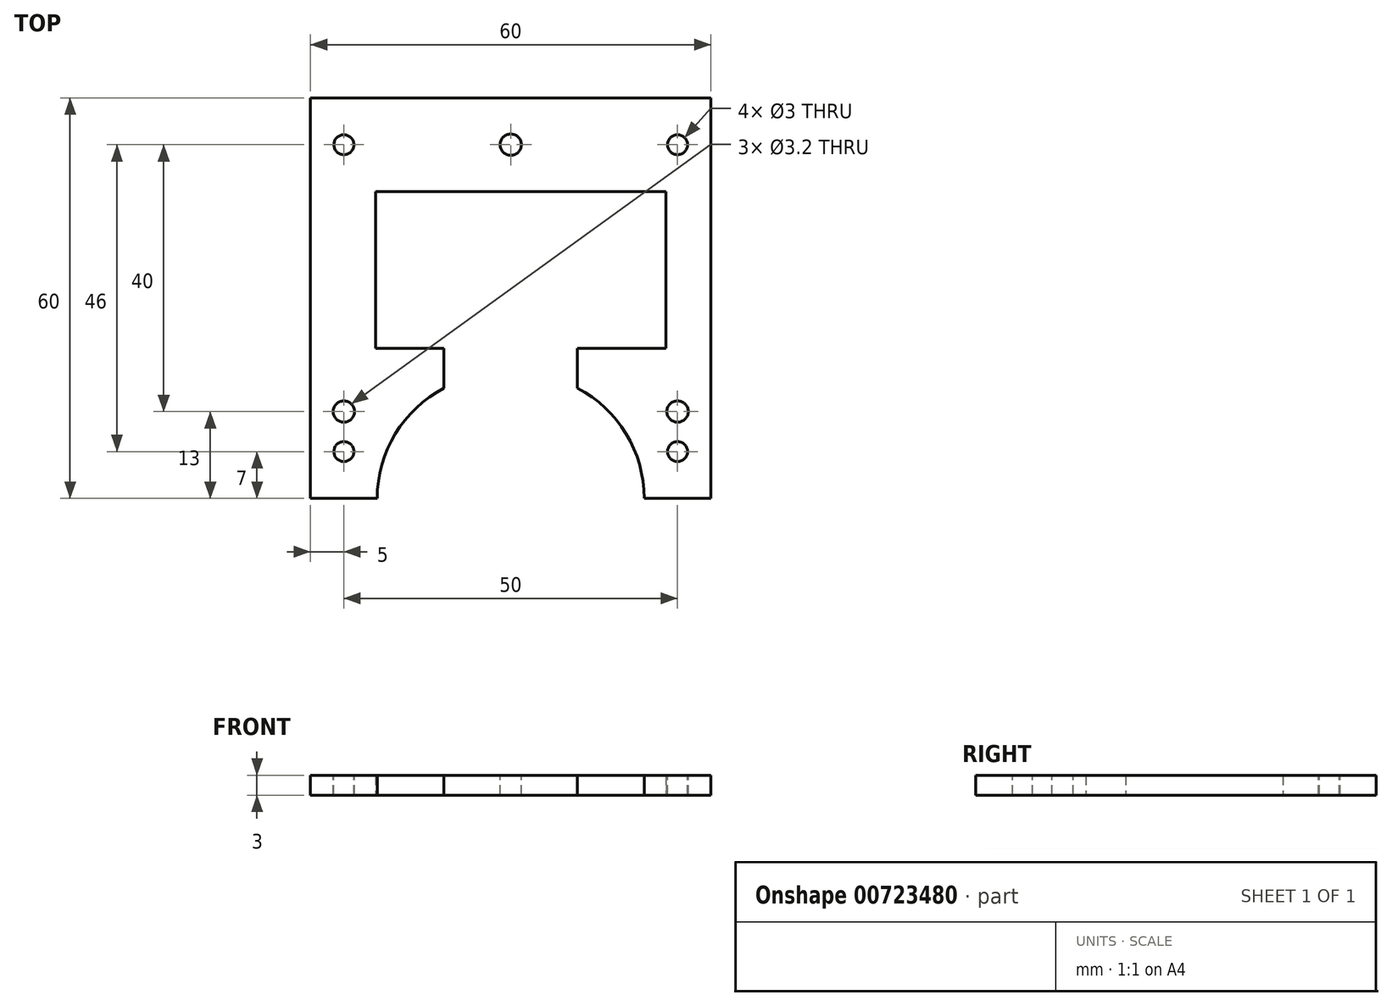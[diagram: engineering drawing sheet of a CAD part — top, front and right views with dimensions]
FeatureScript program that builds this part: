
annotation { "Feature Type Name" : "Feature", "Feature Type Description" : "" }
export const myFeature = defineFeature(function(context is Context, id is Id, definition is map)
    precondition{}
    {
        {
            var Q0;
            Q0=qCreatedBy(makeId("Top.planeOp"),FACE);
            var sketch = newSketch(context, id + "F0", { "sketchPlane" : qUnion([Q0])});
            skLineSegment(sketch, "E0.bottom", {"start": v(30, 30) * mm, "end": v(-30, 30) * mm});
            skLineSegment(sketch, "E0.top", {"start": v(30, -30) * mm, "end": v(20, -30) * mm});
            skLineSegment(sketch, "E0.left", {"start": v(30, 30) * mm, "end": v(30, -30) * mm});
            skLineSegment(sketch, "E0.right", {"start": v(-30, 30) * mm, "end": v(-30, -30) * mm});
            skPoint(sketch, "E0.middle", {"position": v(0, 0) * mm});
            skLineSegment(sketch, "E1.bottom", {"start": v(20, 15.5) * mm, "end": v(-20, 15.5) * mm});
            skLineSegment(sketch, "E1.left", {"start": v(20, 15.5) * mm, "end": v(20, -7.5) * mm});
            skLineSegment(sketch, "E1.right", {"start": v(-20, 15.5) * mm, "end": v(-20, -7.5) * mm});
            skLineSegment(sketch, "E2", {"start": v(-20, -7.5) * mm, "end": v(-10, -7.5) * mm});
            skLineSegment(sketch, "E3", {"start": v(10, -7.5) * mm, "end": v(20, -7.5) * mm});
            skPoint(sketch, "E4.orphan", {"position": v(-20, -15.5) * mm});
            skPoint(sketch, "E5.orphan", {"position": v(20, -15.5) * mm});
            skLineSegment(sketch, "E6", {"start": v(-20, -15.5) * mm, "end": v(-20, -30) * mm});
            skLineSegment(sketch, "E7", {"start": v(20, -30) * mm, "end": v(20, -15.5) * mm});
            skLineSegment(sketch, "E8", {"start": v(-10, -7.5) * mm, "end": v(-10, -13.5) * mm});
            skLineSegment(sketch, "E9.trimOffspring", {"start": v(-20, -30) * mm, "end": v(-30, -30) * mm});
            skLineSegment(sketch, "E10", {"start": v(-10, -13.5) * mm, "end": v(-19.98, -13.5) * mm});
            skLineSegment(sketch, "E11", {"start": v(-19.98, -13.5) * mm, "end": v(-20, -15.5) * mm});
            skLineSegment(sketch, "E12", {"start": v(10, -7.5) * mm, "end": v(10, -13.5) * mm});
            skLineSegment(sketch, "E13", {"start": v(10, -13.5) * mm, "end": v(20, -13.5) * mm});
            skLineSegment(sketch, "E14", {"start": v(20, -13.5) * mm, "end": v(20, -15.5) * mm});
            skArc(sketch, "E15", {"start": v(-10, -13.5) * mm, "mid": v(-17.3, -20.35) * mm, "end": v(-20, -30) * mm});
            skArc(sketch, "E16", {"start": v(20, -30) * mm, "mid": v(17.3, -20.35) * mm, "end": v(10, -13.5) * mm});
            skSolve(sketch);
        }
        {
            var Q0;
            Q0=makeQuery(id+"F0.imprint","IMPRINT",FACE,{"disambiguationData":[TD([[makeQuery(id+"F0.imprint","IMPRINT",EDGE,{"derivedFrom":sQuery(id+"F0.wireOp",EDGE,"E0.bottom")}),1.0]])]});
            var Q1;
            Q1=makeQuery(id+"F0.imprint","IMPRINT",FACE,{"disambiguationData":[TD([[makeQuery(id+"F0.imprint","IMPRINT",EDGE,{"derivedFrom":sQuery(id+"F0.wireOp",EDGE,"E6")}),1.0]])]});
            var Q2;
            Q2=makeQuery(id+"F0.imprint","IMPRINT",FACE,{"disambiguationData":[TD([[makeQuery(id+"F0.imprint","IMPRINT",EDGE,{"derivedFrom":sQuery(id+"F0.wireOp",EDGE,"E7")}),1.0]])]});
            extrude(context, id + "F1", {"entities" : qUnion([Q0, Q1, Q2]), "depth" : 3 * mm, "offsetDistance" : 25 * mm});
        }
        {
            var Q0;
            Q0=makeQuery(id+"F1.opExtrude","CAP_FACE",FACE,{"disambiguationData":[OSD([sQuery(id+"F0.wireOp",EDGE,"E0.bottom"),sQuery(id+"F0.wireOp",EDGE,"E0.top"),sQuery(id+"F0.wireOp",EDGE,"E0.left"),sQuery(id+"F0.wireOp",EDGE,"E0.right"),sQuery(id+"F0.wireOp",EDGE,"E1.bottom"),sQuery(id+"F0.wireOp",EDGE,"E1.left"),sQuery(id+"F0.wireOp",EDGE,"E1.right"),sQuery(id+"F0.wireOp",EDGE,"E2"),sQuery(id+"F0.wireOp",EDGE,"E3"),sQuery(id+"F0.wireOp",EDGE,"E6"),sQuery(id+"F0.wireOp",EDGE,"E7"),sQuery(id+"F0.wireOp",EDGE,"E8"),sQuery(id+"F0.wireOp",EDGE,"E9.trimOffspring"),sQuery(id+"F0.wireOp",EDGE,"E10"),sQuery(id+"F0.wireOp",EDGE,"E11"),sQuery(id+"F0.wireOp",EDGE,"E12"),sQuery(id+"F0.wireOp",EDGE,"E13"),sQuery(id+"F0.wireOp",EDGE,"E14")])],"isStart":false});
            var sketch = newSketch(context, id + "F2", { "sketchPlane" : qUnion([Q0])});
            skCircle(sketch, "E17", {"center": v(-25, 23) * mm, "radius": 1.5 * mm});
            skCircle(sketch, "E18", {"center": v(25, 23) * mm, "radius": 1.5 * mm});
            skCircle(sketch, "E19", {"center": v(-25, -23) * mm, "radius": 1.5 * mm});
            skCircle(sketch, "E20", {"center": v(25, -23) * mm, "radius": 1.5 * mm});
            skSolve(sketch);
        }
        {
            var Q0;
            Q0 = qSketchRegion(id + "F2", true);
            extrude(context, id + "F3", {"entities" : qUnion([Q0]), "operationType" : NewBodyOperationType.REMOVE, "endBound" : BoundingType.THROUGH_ALL, "oppositeDirection" : true, "depth" : 25 * mm, "offsetDistance" : 25 * mm});
        }
        {
            var Q0;
            Q0=makeQuery(id+"F1.opExtrude","CAP_FACE",FACE,{"disambiguationData":[OSD([sQuery(id+"F0.wireOp",EDGE,"E0.bottom"),sQuery(id+"F0.wireOp",EDGE,"E0.top"),sQuery(id+"F0.wireOp",EDGE,"E0.left"),sQuery(id+"F0.wireOp",EDGE,"E0.right"),sQuery(id+"F0.wireOp",EDGE,"E1.bottom"),sQuery(id+"F0.wireOp",EDGE,"E1.left"),sQuery(id+"F0.wireOp",EDGE,"E1.right"),sQuery(id+"F0.wireOp",EDGE,"E2"),sQuery(id+"F0.wireOp",EDGE,"E3"),sQuery(id+"F0.wireOp",EDGE,"E8"),sQuery(id+"F0.wireOp",EDGE,"E9.trimOffspring"),sQuery(id+"F0.wireOp",EDGE,"E12"),sQuery(id+"F0.wireOp",EDGE,"E15"),sQuery(id+"F0.wireOp",EDGE,"E16")])],"isStart":false});
            var sketch = newSketch(context, id + "F4", { "sketchPlane" : qUnion([Q0])});
            skCircle(sketch, "E21", {"center": v(25, -17) * mm, "radius": 1.6 * mm});
            skCircle(sketch, "E22", {"center": v(-25, -17) * mm, "radius": 1.6 * mm});
            skCircle(sketch, "E23", {"center": v(0, 23) * mm, "radius": 1.6 * mm});
            skSolve(sketch);
        }
        {
            var Q0;
            Q0 = qSketchRegion(id + "F4", true);
            extrude(context, id + "F5", {"entities" : qUnion([Q0]), "operationType" : NewBodyOperationType.REMOVE, "endBound" : BoundingType.THROUGH_ALL, "oppositeDirection" : true, "depth" : 25 * mm, "offsetDistance" : 25 * mm});
        }
        {
            var Q0;
            Q0=makeQuery(id+"F1.opExtrude","SWEPT_FACE",FACE,{"disambiguationData":[OSD([sQuery(id+"F0.wireOp",EDGE,"E1.bottom")])]});
            var sketch = newSketch(context, id + "F6", { "sketchPlane" : qUnion([Q0])});
            skLineSegment(sketch, "E24.bottom", {"start": v(-20, 0) * mm, "end": v(20, 0) * mm});
            skLineSegment(sketch, "E24.top", {"start": v(-20, 3) * mm, "end": v(20, 3) * mm});
            skLineSegment(sketch, "E24.left", {"start": v(-20, 0) * mm, "end": v(-20, 3) * mm});
            skLineSegment(sketch, "E24.right", {"start": v(20, 0) * mm, "end": v(20, 3) * mm});
            skSolve(sketch);
        }
        {
            var Q0;
            Q0 = qSketchRegion(id + "F6", true);
            extrude(context, id + "F7", {"entities" : qUnion([Q0]), "operationType" : NewBodyOperationType.REMOVE, "oppositeDirection" : true, "depth" : 0.5 * mm, "offsetDistance" : 25 * mm});
        }
        {
            var Q0;
            Q0=makeQuery(id+"F7.boolean.opBoolean","MERGE",FACE,{"derivedFrom":[makeQuery(id+"F1.opExtrude","SWEPT_FACE",FACE,{"disambiguationData":[OSD([sQuery(id+"F0.wireOp",EDGE,"E1.right")])]}),makeQuery(id+"F7.opExtrude","SWEPT_FACE",FACE,{"disambiguationData":[OSD([sQuery(id+"F6.wireOp",EDGE,"E24.left")])]})]});
            var sketch = newSketch(context, id + "F8", { "sketchPlane" : qUnion([Q0])});
            skLineSegment(sketch, "E25.bottom", {"start": v(16, 3) * mm, "end": v(-7.5, 3) * mm});
            skLineSegment(sketch, "E25.top", {"start": v(16, 0) * mm, "end": v(-7.5, 0) * mm});
            skLineSegment(sketch, "E25.left", {"start": v(16, 3) * mm, "end": v(16, 0) * mm});
            skLineSegment(sketch, "E25.right", {"start": v(-7.5, 3) * mm, "end": v(-7.5, 0) * mm});
            skSolve(sketch);
        }
        {
            var Q0;
            Q0 = qSketchRegion(id + "F8", true);
            extrude(context, id + "F9", {"entities" : qUnion([Q0]), "operationType" : NewBodyOperationType.REMOVE, "oppositeDirection" : true, "depth" : 0.25 * mm, "offsetDistance" : 25 * mm});
        }
        {
            var Q0;
            Q0=makeQuery(id+"F7.boolean.opBoolean","MERGE",FACE,{"derivedFrom":[makeQuery(id+"F1.opExtrude","SWEPT_FACE",FACE,{"disambiguationData":[OSD([sQuery(id+"F0.wireOp",EDGE,"E1.left")])]}),makeQuery(id+"F7.opExtrude","SWEPT_FACE",FACE,{"disambiguationData":[OSD([sQuery(id+"F6.wireOp",EDGE,"E24.right")])]})]});
            var sketch = newSketch(context, id + "F10", { "sketchPlane" : qUnion([Q0])});
            skLineSegment(sketch, "E26.bottom", {"start": v(-16, 3) * mm, "end": v(7.5, 3) * mm});
            skLineSegment(sketch, "E26.top", {"start": v(-16, 0) * mm, "end": v(7.5, 0) * mm});
            skLineSegment(sketch, "E26.left", {"start": v(-16, 3) * mm, "end": v(-16, 0) * mm});
            skLineSegment(sketch, "E26.right", {"start": v(7.5, 3) * mm, "end": v(7.5, 0) * mm});
            skSolve(sketch);
        }
        {
            var Q0;
            Q0 = qSketchRegion(id + "F10", true);
            extrude(context, id + "F11", {"entities" : qUnion([Q0]), "operationType" : NewBodyOperationType.REMOVE, "oppositeDirection" : true, "depth" : 0.25 * mm, "offsetDistance" : 25 * mm});
        }
        {
            var Q0;
            Q0=makeQuery(id+"F11.boolean.opBoolean","COPY",FACE,{"derivedFrom":makeQuery(id+"F11.opExtrude","CAP_FACE",FACE,{"disambiguationData":[OSD([sQuery(id+"F10.wireOp",EDGE,"E26.bottom"),sQuery(id+"F10.wireOp",EDGE,"E26.top"),sQuery(id+"F10.wireOp",EDGE,"E26.left"),sQuery(id+"F10.wireOp",EDGE,"E26.right")])],"isStart":false})});
            var sketch = newSketch(context, id + "F12", { "sketchPlane" : qUnion([Q0])});
            skLineSegment(sketch, "E27.bottom", {"start": v(-16, 3) * mm, "end": v(7.5, 3) * mm});
            skLineSegment(sketch, "E27.top", {"start": v(-16, 0) * mm, "end": v(7.5, 0) * mm});
            skLineSegment(sketch, "E27.left", {"start": v(-16, 3) * mm, "end": v(-16, 0) * mm});
            skLineSegment(sketch, "E27.right", {"start": v(7.5, 3) * mm, "end": v(7.5, 0) * mm});
            skSolve(sketch);
        }
        {
            var Q0;
            Q0 = qSketchRegion(id + "F12", true);
            extrude(context, id + "F13", {"entities" : qUnion([Q0]), "operationType" : NewBodyOperationType.REMOVE, "oppositeDirection" : true, "depth" : 3 * mm, "offsetDistance" : 25 * mm});
        }
    });
